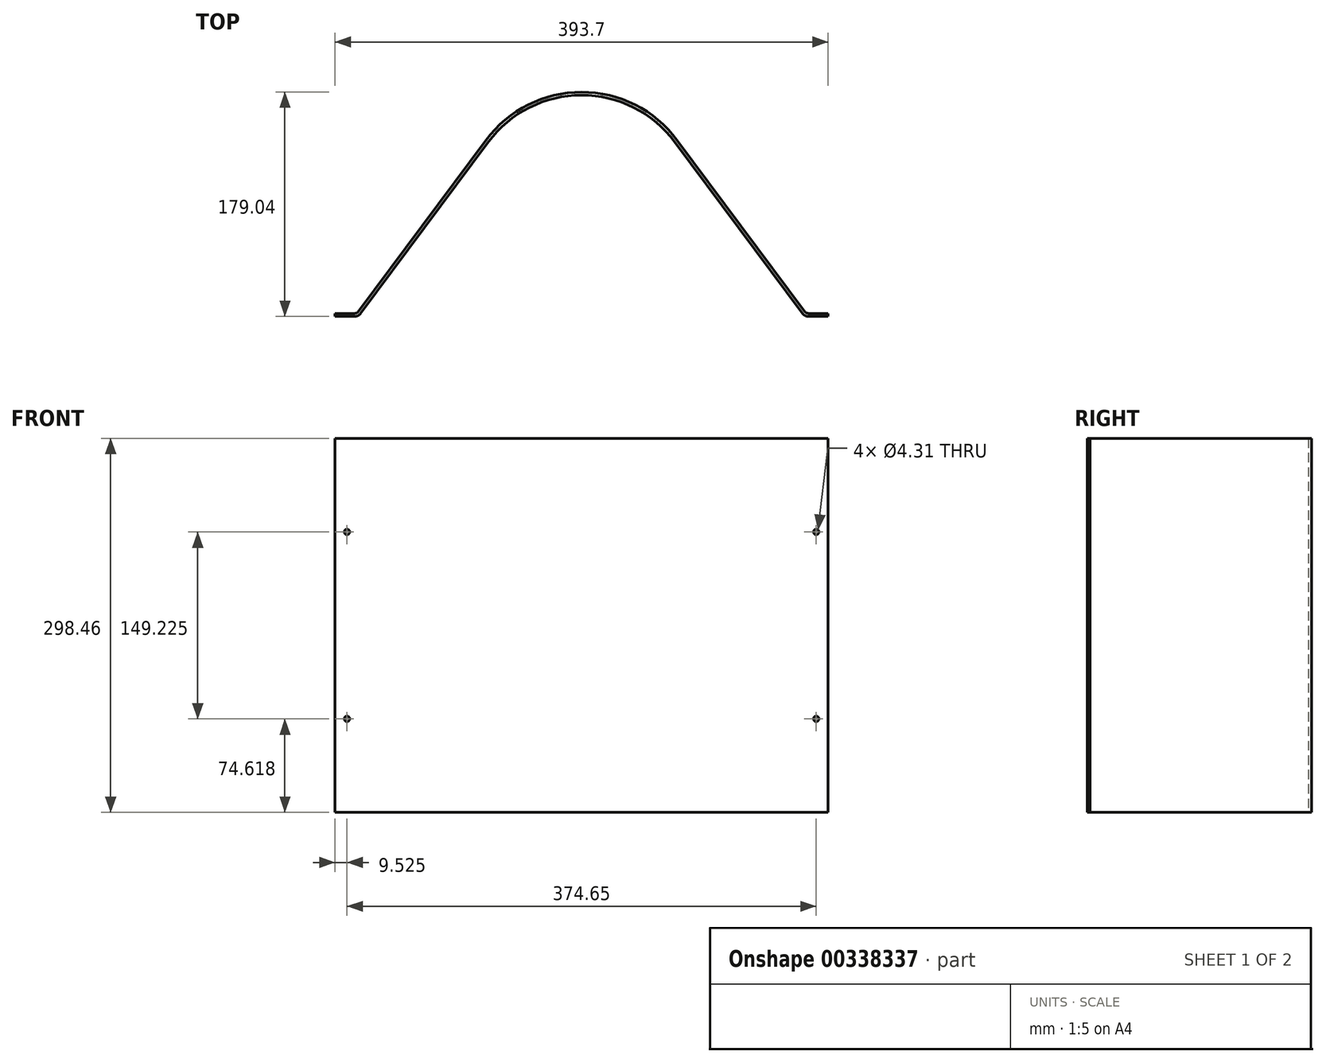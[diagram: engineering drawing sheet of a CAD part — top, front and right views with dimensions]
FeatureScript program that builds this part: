
annotation { "Feature Type Name" : "Feature", "Feature Type Description" : "" }
export const myFeature = defineFeature(function(context is Context, id is Id, definition is map)
    precondition{}
    {
        {
            var Q0;
            Q0=qCreatedBy(makeId("Top.planeOp"),FACE);
            var sketch = newSketch(context, id + "F0", { "sketchPlane" : qUnion([Q0])});
            skLineSegment(sketch, "E0", {"start": v(0, 0) * mm, "end": v(15.88, 0) * mm});
            skLineSegment(sketch, "E1", {"start": v(0, 0) * mm, "end": v(0, -2.38) * mm});
            skLineSegment(sketch, "E2", {"start": v(0, -2.38) * mm, "end": v(393.7, -2.38) * mm});
            skArc(sketch, "E3", {"start": v(15.88, 0) * mm, "mid": v(17.3, 0.34) * mm, "end": v(18.42, 1.28) * mm});
            skLineSegment(sketch, "E4", {"start": v(393.7, -2.38) * mm, "end": v(393.7, 0) * mm});
            skLineSegment(sketch, "E5", {"start": v(393.7, 0) * mm, "end": v(377.83, 0) * mm});
            skLineSegment(sketch, "E6", {"start": v(196.85, -2.38) * mm, "end": v(196.85, 81.57) * mm, "construction": true});
            skArc(sketch, "E7", {"start": v(375.28, 1.28) * mm, "mid": v(376.4, 0.34) * mm, "end": v(377.83, 0) * mm});
            skArc(sketch, "E8", {"start": v(273.1, 138.39) * mm, "mid": v(196.85, 176.66) * mm, "end": v(120.6, 138.39) * mm});
            skLineSegment(sketch, "E9", {"start": v(273.1, 138.39) * mm, "end": v(375.28, 1.28) * mm});
            skLineSegment(sketch, "E10", {"start": v(120.6, 138.39) * mm, "end": v(18.42, 1.28) * mm});
            skSolve(sketch);
        }
        {
            var Q0;
            Q0=qSketchRegion(id+"F0",true);
            extrude(context, id + "F1", {"entities" : qUnion([Q0]), "depth" : 609.6 * mm});
        }
        {
            var Q0;
            Q0=makeQuery(id+"F1.opExtrude","SWEPT_FACE",FACE,{"disambiguationData":[OSD([sQuery(id+"F0.wireOp",EDGE,"E2")])]});
            shell(context, id + "F2", {"entities" : qUnion([Q0]), "thickness" : 2.38 * mm});
        }
        {
            var Q0;
            Q0=makeQuery(id+"F1.opExtrude","SWEPT_FACE",FACE,{"disambiguationData":[OSD([sQuery(id+"F0.wireOp",EDGE,"E2")])]});
            var sketch = newSketch(context, id + "F3", { "sketchPlane" : qUnion([Q0])});
            skLineSegment(sketch, "E11.bottom", {"start": v(0, 609.6) * mm, "end": v(393.7, 609.6) * mm});
            skLineSegment(sketch, "E11.top", {"start": v(0, 454.03) * mm, "end": v(393.7, 454.03) * mm});
            skLineSegment(sketch, "E11.left", {"start": v(0, 609.6) * mm, "end": v(0, 454.03) * mm});
            skLineSegment(sketch, "E11.right", {"start": v(393.7, 609.6) * mm, "end": v(393.7, 454.03) * mm});
            skLineSegment(sketch, "E12.bottom", {"start": v(393.7, 0) * mm, "end": v(0, 0) * mm});
            skLineSegment(sketch, "E12.top", {"start": v(393.7, 155.57) * mm, "end": v(0, 155.57) * mm});
            skLineSegment(sketch, "E12.left", {"start": v(393.7, 0) * mm, "end": v(393.7, 155.57) * mm});
            skLineSegment(sketch, "E12.right", {"start": v(0, 0) * mm, "end": v(0, 155.57) * mm});
            skLineSegment(sketch, "E13", {"start": v(196.85, 454.03) * mm, "end": v(196.85, 155.57) * mm, "construction": true});
            skSolve(sketch);
        }
        {
            var Q0;
            Q0=qSketchRegion(id+"F3",true);
            var Q1;
            Q1=makeQuery(id+"F1.opExtrude","SWEPT_FACE",FACE,{"disambiguationData":[OSD([sQuery(id+"F0.wireOp",EDGE,"E10")])]});
            extrude(context, id + "F4", {"entities" : qUnion([Q0]), "operationType" : NewBodyOperationType.REMOVE, "endBound" : BoundingType.THROUGH_ALL, "oppositeDirection" : true, "endBoundEntityFace" : qUnion([Q1]), "depth" : 25.4 * mm});
        }
        {
            var Q0;
            Q0=makeQuery(id+"F4.boolean.opBoolean","SPLIT",FACE,{"disambiguationData":[TD([makeQuery(id+"F1.opExtrude","SWEPT_FACE",FACE,{"disambiguationData":[OSD([sQuery(id+"F0.wireOp",EDGE,"E4")])]})])],"derivedFrom":makeQuery(id+"F1.opExtrude","SWEPT_FACE",FACE,{"disambiguationData":[OSD([sQuery(id+"F0.wireOp",EDGE,"E2")])]})});
            var sketch = newSketch(context, id + "F5", { "sketchPlane" : qUnion([Q0])});
            skLineSegment(sketch, "E14", {"start": v(384.18, 454.03) * mm, "end": v(384.18, 379.41) * mm, "construction": true});
            skLineSegment(sketch, "E15", {"start": v(384.18, 379.41) * mm, "end": v(384.18, 304.8) * mm, "construction": true});
            skLineSegment(sketch, "E16", {"start": v(384.18, 304.8) * mm, "end": v(384.18, 230.19) * mm, "construction": true});
            skLineSegment(sketch, "E17", {"start": v(384.18, 230.19) * mm, "end": v(384.18, 155.57) * mm, "construction": true});
            skCircle(sketch, "E18", {"center": v(384.18, 230.19) * mm, "radius": 2.15 * mm});
            skCircle(sketch, "E19", {"center": v(384.18, 379.41) * mm, "radius": 2.15 * mm});
            skLineSegment(sketch, "E20", {"start": v(384.18, 304.8) * mm, "end": v(393.7, 304.8) * mm, "construction": true});
            skLineSegment(sketch, "E21", {"start": v(196.85, 454.03) * mm, "end": v(196.85, 155.58) * mm, "construction": true});
            skLineSegment(sketch, "E22", {"start": v(0, 304.8) * mm, "end": v(9.53, 304.8) * mm, "construction": true});
            skLineSegment(sketch, "E23", {"start": v(9.53, 304.8) * mm, "end": v(9.53, 379.41) * mm, "construction": true});
            skLineSegment(sketch, "E24", {"start": v(9.53, 304.8) * mm, "end": v(9.53, 230.19) * mm, "construction": true});
            skCircle(sketch, "E25", {"center": v(9.53, 379.41) * mm, "radius": 2.15 * mm});
            skCircle(sketch, "E26", {"center": v(9.53, 230.19) * mm, "radius": 2.15 * mm});
            skSolve(sketch);
        }
        {
            var Q0;
            Q0=qSketchRegion(id+"F5",true);
            var Q1;
            Q1=makeQuery(id+"F1.opExtrude","SWEPT_FACE",FACE,{"disambiguationData":[OSD([sQuery(id+"F0.wireOp",EDGE,"E5")])]});
            extrude(context, id + "F6", {"entities" : qUnion([Q0]), "operationType" : NewBodyOperationType.REMOVE, "endBound" : BoundingType.UP_TO_SURFACE, "oppositeDirection" : true, "endBoundEntityFace" : qUnion([Q1]), "depth" : 25.4 * mm});
        }
    });
